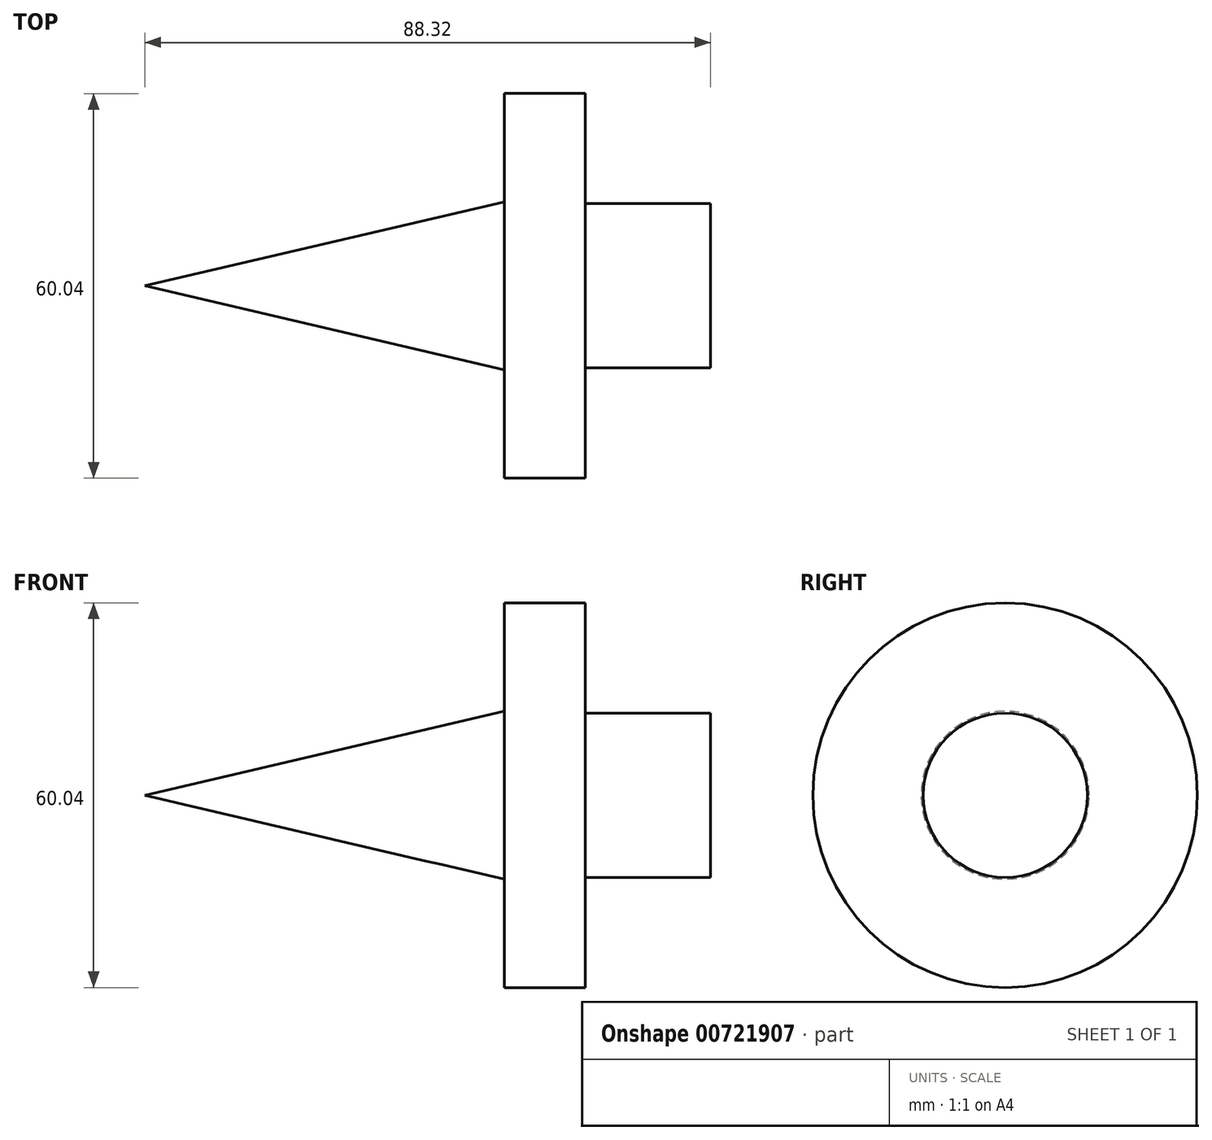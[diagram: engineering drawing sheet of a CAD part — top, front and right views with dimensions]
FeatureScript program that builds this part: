
annotation { "Feature Type Name" : "Feature", "Feature Type Description" : "" }
export const myFeature = defineFeature(function(context is Context, id is Id, definition is map)
    precondition{}
    {
        {
            var Q0;
            Q0=qCreatedBy(makeId("Top.planeOp"),FACE);
            var sketch = newSketch(context, id + "F0", { "sketchPlane" : qUnion([Q0])});
            skLineSegment(sketch, "E0", {"start": v(-56.1, 0) * mm, "end": v(0, 13.12) * mm});
            skLineSegment(sketch, "E1", {"start": v(0, 13.12) * mm, "end": v(0, 30.02) * mm});
            skLineSegment(sketch, "E2", {"start": v(0, 30.02) * mm, "end": v(12.68, 30.02) * mm});
            skLineSegment(sketch, "E3", {"start": v(12.68, 30.02) * mm, "end": v(12.68, 12.82) * mm});
            skLineSegment(sketch, "E4", {"start": v(12.68, 12.82) * mm, "end": v(32.2, 12.82) * mm});
            skLineSegment(sketch, "E5", {"start": v(32.2, 12.82) * mm, "end": v(32.2, 0) * mm});
            skLineSegment(sketch, "E6", {"start": v(32.2, 0) * mm, "end": v(-56.1, 0) * mm});
            skSolve(sketch);
        }
        {
            var Q0;
            Q0=makeQuery(id+"F0.imprint","IMPRINT",FACE,{"disambiguationData":[TD([[makeQuery(id+"F0.imprint","IMPRINT",EDGE,{"derivedFrom":sQuery(id+"F0.wireOp",EDGE,"E0")}),-1.0]])]});
            var Q1;
            Q1=sQuery(id+"F0.wireOp",EDGE,"E6");
            revolve(context, id + "F1", {"surfaceOperationType" : NewSurfaceOperationType.NEW, "entities" : qUnion([Q0]), "axis" : qUnion([Q1]), "revolveType" : RevolveType.FULL});
        }
    });
